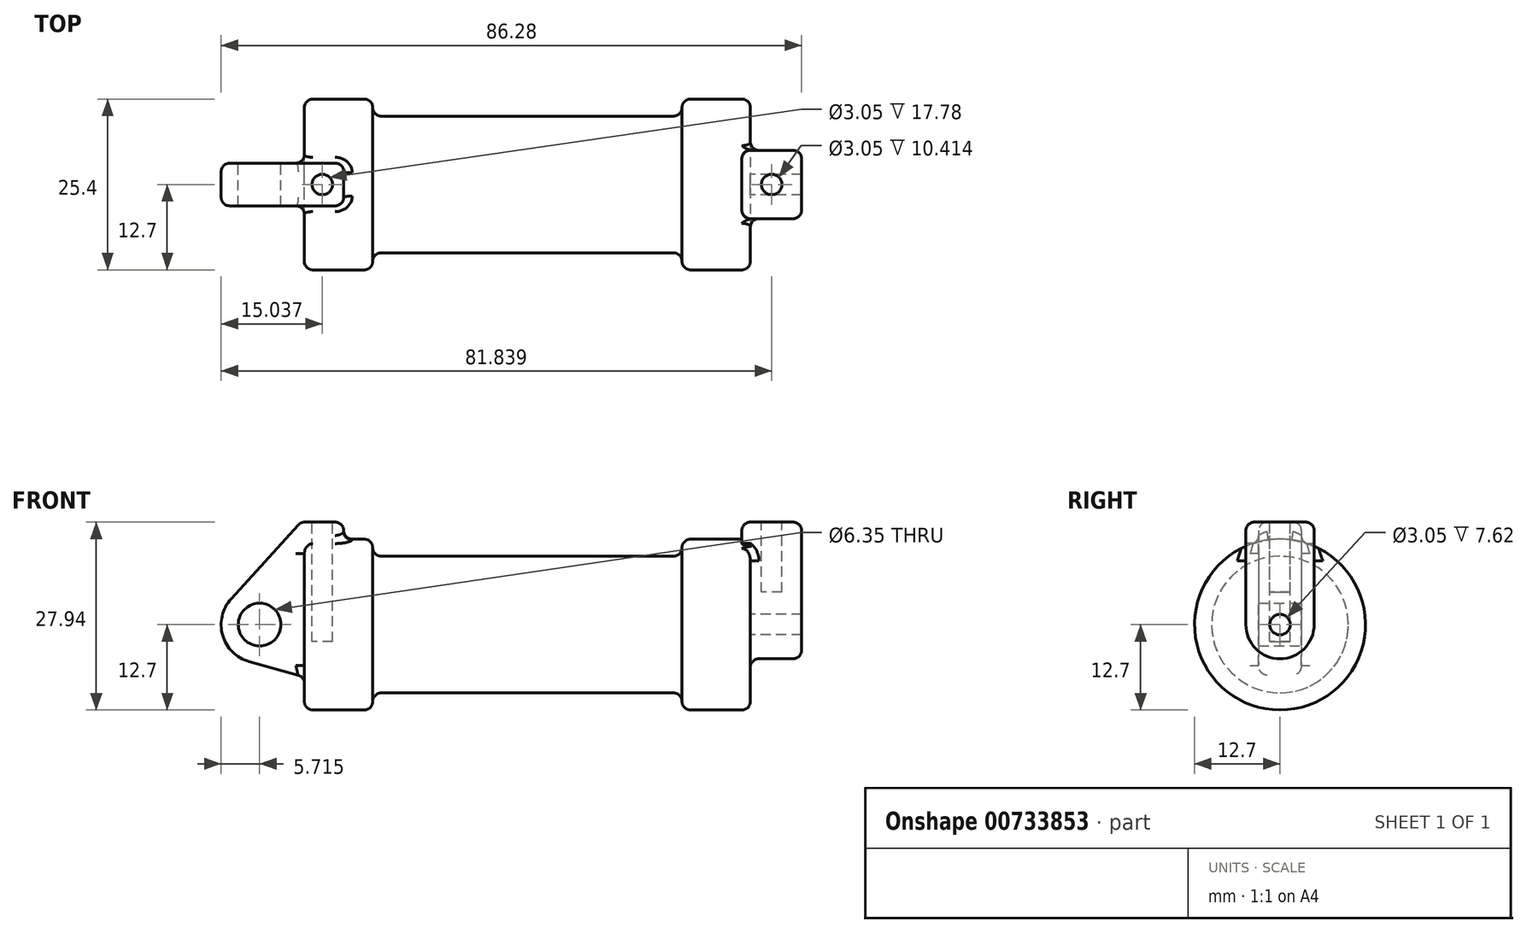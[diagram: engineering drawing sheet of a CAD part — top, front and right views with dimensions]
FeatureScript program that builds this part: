
annotation { "Feature Type Name" : "Feature", "Feature Type Description" : "" }
export const myFeature = defineFeature(function(context is Context, id is Id, definition is map)
    precondition{}
    {
        {
            var Q0;
            Q0=qCreatedBy(makeId("Front.planeOp"),FACE);
            var sketch = newSketch(context, id + "F0", { "sketchPlane" : qUnion([Q0])});
            skLineSegment(sketch, "E0", {"start": v(0, 0) * mm, "end": v(0, 12.7) * mm});
            skLineSegment(sketch, "E1", {"start": v(0, 12.7) * mm, "end": v(10.16, 12.7) * mm});
            skLineSegment(sketch, "E2", {"start": v(10.16, 12.7) * mm, "end": v(10.16, 10.16) * mm});
            skLineSegment(sketch, "E3", {"start": v(10.16, 10.16) * mm, "end": v(56.13, 10.16) * mm});
            skLineSegment(sketch, "E4", {"start": v(56.13, 10.16) * mm, "end": v(56.13, 12.7) * mm});
            skLineSegment(sketch, "E5", {"start": v(56.13, 12.7) * mm, "end": v(66.3, 12.7) * mm});
            skLineSegment(sketch, "E6", {"start": v(66.3, 12.7) * mm, "end": v(66.3, 0) * mm});
            skLineSegment(sketch, "E7", {"start": v(66.3, 0) * mm, "end": v(0, 0) * mm});
            skLineSegment(sketch, "E8", {"start": v(5.84, 15.24) * mm, "end": v(-0.5, 15.24) * mm});
            skLineSegment(sketch, "E9", {"start": v(-0.5, 15.24) * mm, "end": v(-10.88, 3.85) * mm});
            skLineSegment(sketch, "E10", {"start": v(0, 0) * mm, "end": v(-6.65, 0) * mm});
            skCircle(sketch, "E11", {"center": v(-6.65, 0) * mm, "radius": 5.72 * mm});
            skCircle(sketch, "E12", {"center": v(-6.65, 0) * mm, "radius": 3.18 * mm});
            skLineSegment(sketch, "E13", {"start": v(5.84, 15.24) * mm, "end": v(5.84, -9.4) * mm});
            skLineSegment(sketch, "E14", {"start": v(5.84, -9.4) * mm, "end": v(-8.18, -5.5) * mm});
            skSolve(sketch);
        }
        {
            var Q0;
            {var subQ0=sQuery(id+"F0.wireOp",EDGE,"E0");Q0=makeQuery(id+"F0.imprint","IMPRINT",FACE,{"disambiguationData":[TD([[makeQuery(id+"F0.imprint","IMPRINT",EDGE,{"derivedFrom":subQ0}),-1.0]])]});}
            var Q1;
            {var subQ0=sQuery(id+"F0.wireOp",EDGE,"E2");Q1=makeQuery(id+"F0.imprint","IMPRINT",FACE,{"disambiguationData":[TD([[makeQuery(id+"F0.imprint","IMPRINT",EDGE,{"derivedFrom":subQ0}),-1.0]])]});}
            var Q2;
            Q2=sQuery(id+"F0.wireOp",EDGE,"E10");
            revolve(context, id + "F1", {"surfaceOperationType" : NewSurfaceOperationType.NEW, "entities" : qUnion([Q0, Q1]), "axis" : qUnion([Q2]), "revolveType" : RevolveType.FULL});
        }
        {
            var Q0;
            {var subQ0=sQuery(id+"F0.wireOp",EDGE,"E0");Q0=makeQuery(id+"F0.imprint","IMPRINT",FACE,{"disambiguationData":[TD([[makeQuery(id+"F0.imprint","IMPRINT",EDGE,{"derivedFrom":subQ0}),-1.0]])]});}
            var Q1;
            {var subQ1=sQuery(id+"F0.wireOp",EDGE,"E0");Q1=makeQuery(id+"F0.imprint","IMPRINT",FACE,{"disambiguationData":[TD([[makeQuery(id+"F0.imprint","IMPRINT",EDGE,{"derivedFrom":subQ1}),1.0]])]});}
            var Q2;
            {var subQ5=sQuery(id+"F0.wireOp",EDGE,"E12");Q2=makeQuery(id+"F0.imprint","IMPRINT",FACE,{"disambiguationData":[TD([[makeQuery(id+"F0.imprint","IMPRINT",EDGE,{"derivedFrom":subQ5}),-1.0]])]});}
            var Q3;
            {var subQ0=sQuery(id+"F0.wireOp",EDGE,"E14");Q3=makeQuery(id+"F0.imprint","IMPRINT",FACE,{"disambiguationData":[TD([[makeQuery(id+"F0.imprint","IMPRINT",EDGE,{"derivedFrom":subQ0}),-1.0]])]});}
            extrude(context, id + "F2", {"entities" : qUnion([Q0, Q1, Q2, Q3]), "operationType" : NewBodyOperationType.ADD, "endBound" : BoundingType.SYMMETRIC, "depth" : 6.35 * mm, "offsetDistance" : 25.4 * mm});
        }
        {
            var Q0;
            Q0=makeQuery(id+"F1.opRevolve","SWEPT_FACE",FACE,{"disambiguationData":[OSD([sQuery(id+"F0.wireOp",EDGE,"E6")])]});
            var sketch = newSketch(context, id + "F3", { "sketchPlane" : qUnion([Q0])});
            skCircle(sketch, "E15", {"center": v(0, 0) * mm, "radius": 1.52 * mm});
            skCircle(sketch, "E16", {"center": v(0, 0) * mm, "radius": 5.08 * mm});
            skLineSegment(sketch, "E17", {"start": v(5.08, 0) * mm, "end": v(5.08, 15.24) * mm});
            skLineSegment(sketch, "E18", {"start": v(5.08, 15.24) * mm, "end": v(-5.08, 15.24) * mm});
            skLineSegment(sketch, "E19", {"start": v(-5.08, 15.24) * mm, "end": v(-5.08, 0) * mm});
            skSolve(sketch);
        }
        {
            var Q0;
            Q0=makeQuery(id+"F3.imprint","IMPRINT",FACE,{"disambiguationData":[TD([[makeQuery(id+"F3.imprint","IMPRINT",EDGE,{"derivedFrom":sQuery(id+"F3.wireOp",EDGE,"E15")}),-1.0]])]});
            var Q1;
            {var subQ0=sQuery(id+"F3.wireOp",EDGE,"E18");Q1=makeQuery(id+"F3.imprint","IMPRINT",FACE,{"disambiguationData":[TD([[makeQuery(id+"F3.imprint","IMPRINT",EDGE,{"derivedFrom":subQ0}),1.0]])]});}
            var Q2;
            {var subQ0=sQuery(id+"F3.wireOp",EDGE,"E17");var subQ1=sQuery(id+"F3.wireOp",EDGE,"E16");var subQ2=makeQuery(id+"F3.imprint","INTERSECT",VERTEX,{"derivedFrom":[subQ1,subQ0]});Q2=makeQuery(id+"F3.imprint","IMPRINT",FACE,{"disambiguationData":[TD([[makeQuery(id+"F3.imprint","IMPRINT",EDGE,{"disambiguationData":[TD([[subQ2,-1.0]])],"derivedFrom":subQ1}),-1.0]])]});}
            extrude(context, id + "F4", {"entities" : qUnion([Q0, Q1, Q2]), "operationType" : NewBodyOperationType.ADD, "depth" : 7.62 * mm, "offsetDistance" : 25.4 * mm, "hasSecondDirection" : true, "secondDirectionOppositeDirection" : true, "secondDirectionDepth" : 1.27 * mm});
        }
        {
            var Q0;
            Q0=makeQuery(id+"F4.opExtrude","SWEPT_FACE",FACE,{"disambiguationData":[OSD([sQuery(id+"F3.wireOp",EDGE,"E18")])]});
            var sketch = newSketch(context, id + "F5", { "sketchPlane" : qUnion([Q0])});
            skCircle(sketch, "E20", {"center": v(69.47, 0) * mm, "radius": 1.52 * mm});
            skPoint(sketch, "E20.centerSnap0", {"position": v(65.02, 0) * mm});
            skPoint(sketch, "E20.centerSnap1", {"position": v(69.47, 5.08) * mm});
            skSolve(sketch);
        }
        {
            var Q0;
            Q0=makeQuery(id+"F2.opExtrude","SWEPT_FACE",FACE,{"disambiguationData":[OSD([sQuery(id+"F0.wireOp",EDGE,"E8")])]});
            var sketch = newSketch(context, id + "F6", { "sketchPlane" : qUnion([Q0])});
            skCircle(sketch, "E21", {"center": v(2.67, 0) * mm, "radius": 1.52 * mm});
            skPoint(sketch, "E21.centerSnap0", {"position": v(5.84, 0) * mm});
            skPoint(sketch, "E21.centerSnap1", {"position": v(2.67, 3.18) * mm});
            skSolve(sketch);
        }
        {
            var Q0;
            Q0=makeQuery(id+"F6.imprint","IMPRINT",FACE,{"disambiguationData":[TD([[makeQuery(id+"F6.imprint","IMPRINT",EDGE,{"derivedFrom":sQuery(id+"F6.wireOp",EDGE,"E21")}),1.0]])]});
            extrude(context, id + "F7", {"entities" : qUnion([Q0]), "operationType" : NewBodyOperationType.REMOVE, "oppositeDirection" : true, "depth" : 17.78 * mm, "offsetDistance" : 25.4 * mm});
        }
        {
            var Q0;
            Q0=makeQuery(id+"F5.imprint","IMPRINT",FACE,{"disambiguationData":[TD([[makeQuery(id+"F5.imprint","IMPRINT",EDGE,{"derivedFrom":sQuery(id+"F5.wireOp",EDGE,"E20")}),1.0]])]});
            extrude(context, id + "F8", {"entities" : qUnion([Q0]), "operationType" : NewBodyOperationType.REMOVE, "oppositeDirection" : true, "depth" : 10.4 * mm, "offsetDistance" : 25.4 * mm});
        }
        {
            var Q0;
            Q0=makeQuery(id+"F1.opRevolve","SWEPT_EDGE",EDGE,{"disambiguationData":[OSD([sQuery(id+"F0.wireOp",EDGE,"E2"),sQuery(id+"F0.wireOp",EDGE,"E3")])]});
            var Q1;
            Q1=makeQuery(id+"F1.opRevolve","SWEPT_EDGE",EDGE,{"disambiguationData":[OSD([sQuery(id+"F0.wireOp",EDGE,"E1"),sQuery(id+"F0.wireOp",EDGE,"E2")])]});
            var Q2;
            Q2=makeQuery(id+"F1.opRevolve","SWEPT_EDGE",EDGE,{"disambiguationData":[OSD([sQuery(id+"F0.wireOp",EDGE,"E0"),sQuery(id+"F0.wireOp",EDGE,"E1")])]});
            var Q3;
            Q3=makeQuery(id+"F1.opRevolve","SWEPT_EDGE",EDGE,{"disambiguationData":[OSD([sQuery(id+"F0.wireOp",EDGE,"E3"),sQuery(id+"F0.wireOp",EDGE,"E4")])]});
            var Q4;
            Q4=makeQuery(id+"F1.opRevolve","SWEPT_EDGE",EDGE,{"disambiguationData":[OSD([sQuery(id+"F0.wireOp",EDGE,"E4"),sQuery(id+"F0.wireOp",EDGE,"E5")])]});
            var Q5;
            Q5=makeQuery(id+"F1.opRevolve","SWEPT_EDGE",EDGE,{"disambiguationData":[OSD([sQuery(id+"F0.wireOp",EDGE,"E5"),sQuery(id+"F0.wireOp",EDGE,"E6")])]});
            fillet(context, id + "F9", {"entities" : qUnion([Q0, Q1, Q2, Q3, Q4, Q5]), "radius" : 1.27 * mm, "tangentPropagation" : true, "allowEdgeOverflow" : false});
        }
        {
            var Q0;
            Q0=makeQuery(id+"F2.boolean.opBoolean","INTERSECT",EDGE,{"derivedFrom":[makeQuery(id+"F1.opRevolve","SWEPT_FACE",FACE,{"disambiguationData":[OSD([sQuery(id+"F0.wireOp",EDGE,"E1")])]}),makeQuery(id+"F2.opExtrude","CAP_FACE",FACE,{"disambiguationData":[OSD([sQuery(id+"F0.wireOp",EDGE,"E8"),sQuery(id+"F0.wireOp",EDGE,"E9"),sQuery(id+"F0.wireOp",EDGE,"E11"),sQuery(id+"F0.wireOp",EDGE,"E12"),sQuery(id+"F0.wireOp",EDGE,"E13"),sQuery(id+"F0.wireOp",EDGE,"E14")])],"isStart":true})]});
            var Q1;
            Q1=makeQuery(id+"F2.boolean.opBoolean","INTERSECT",EDGE,{"derivedFrom":[makeQuery(id+"F1.opRevolve","SWEPT_FACE",FACE,{"disambiguationData":[OSD([sQuery(id+"F0.wireOp",EDGE,"E1")])]}),makeQuery(id+"F2.opExtrude","SWEPT_FACE",FACE,{"disambiguationData":[OSD([sQuery(id+"F0.wireOp",EDGE,"E13")])]})]});
            var Q2;
            Q2=makeQuery(id+"F2.boolean.opBoolean","INTERSECT",EDGE,{"derivedFrom":[makeQuery(id+"F1.opRevolve","SWEPT_FACE",FACE,{"disambiguationData":[OSD([sQuery(id+"F0.wireOp",EDGE,"E1")])]}),makeQuery(id+"F2.opExtrude","CAP_FACE",FACE,{"disambiguationData":[OSD([sQuery(id+"F0.wireOp",EDGE,"E8"),sQuery(id+"F0.wireOp",EDGE,"E9"),sQuery(id+"F0.wireOp",EDGE,"E11"),sQuery(id+"F0.wireOp",EDGE,"E12"),sQuery(id+"F0.wireOp",EDGE,"E13"),sQuery(id+"F0.wireOp",EDGE,"E14")])],"isStart":false})]});
            var Q3;
            Q3=makeQuery(id+"F2.boolean.opBoolean","INTERSECT",EDGE,{"derivedFrom":[makeQuery(id+"F1.opRevolve","SWEPT_FACE",FACE,{"disambiguationData":[OSD([sQuery(id+"F0.wireOp",EDGE,"E0")])]}),makeQuery(id+"F2.opExtrude","SWEPT_FACE",FACE,{"disambiguationData":[OSD([sQuery(id+"F0.wireOp",EDGE,"E14")])]})]});
            var Q4;
            Q4=makeQuery(id+"F2.opExtrude","CAP_EDGE",EDGE,{"disambiguationData":[OSD([sQuery(id+"F0.wireOp",EDGE,"E14")])],"isStart":false});
            var Q5;
            Q5=makeQuery(id+"F2.opExtrude","CAP_EDGE",EDGE,{"disambiguationData":[OSD([sQuery(id+"F0.wireOp",EDGE,"E14")])],"isStart":true});
            var Q6;
            Q6=makeQuery(id+"F2.opExtrude","CAP_EDGE",EDGE,{"disambiguationData":[OSD([sQuery(id+"F0.wireOp",EDGE,"E8")])],"isStart":false});
            var Q7;
            Q7=makeQuery(id+"F2.opExtrude","CAP_EDGE",EDGE,{"disambiguationData":[OSD([sQuery(id+"F0.wireOp",EDGE,"E8")])],"isStart":true});
            var Q8;
            Q8=makeQuery(id+"F2.opExtrude","SWEPT_EDGE",EDGE,{"disambiguationData":[OSD([sQuery(id+"F0.wireOp",EDGE,"E8"),sQuery(id+"F0.wireOp",EDGE,"E13")])]});
            var Q9;
            Q9=makeQuery(id+"F2.opExtrude","SWEPT_EDGE",EDGE,{"disambiguationData":[OSD([sQuery(id+"F0.wireOp",EDGE,"E8"),sQuery(id+"F0.wireOp",EDGE,"E9")])]});
            var Q10;
            Q10=makeQuery(id+"F2.opExtrude","CAP_EDGE",EDGE,{"disambiguationData":[OSD([sQuery(id+"F0.wireOp",EDGE,"E13")])],"isStart":false});
            var Q11;
            Q11=makeQuery(id+"F2.opExtrude","CAP_EDGE",EDGE,{"disambiguationData":[OSD([sQuery(id+"F0.wireOp",EDGE,"E13")])],"isStart":true});
            fillet(context, id + "F10", {"entities" : qUnion([Q0, Q1, Q2, Q3, Q4, Q5, Q6, Q7, Q8, Q9, Q10, Q11]), "radius" : 1.27 * mm, "tangentPropagation" : true, "allowEdgeOverflow" : false});
        }
        {
            var Q0;
            Q0=makeQuery(id+"F4.opExtrude","CAP_EDGE",EDGE,{"disambiguationData":[OSD([sQuery(id+"F3.wireOp",EDGE,"E16")])],"isStart":false});
            var Q1;
            Q1=makeQuery(id+"F4.opExtrude","SWEPT_EDGE",EDGE,{"disambiguationData":[OSD([sQuery(id+"F3.wireOp",EDGE,"E17"),sQuery(id+"F3.wireOp",EDGE,"E18")])]});
            var Q2;
            Q2=makeQuery(id+"F4.opExtrude","CAP_EDGE",EDGE,{"disambiguationData":[OSD([sQuery(id+"F3.wireOp",EDGE,"E18")])],"isStart":false});
            var Q3;
            Q3=makeQuery(id+"F4.opExtrude","SWEPT_EDGE",EDGE,{"disambiguationData":[OSD([sQuery(id+"F3.wireOp",EDGE,"E18"),sQuery(id+"F3.wireOp",EDGE,"E19")])]});
            var Q4;
            Q4=makeQuery(id+"F4.opExtrude","CAP_EDGE",EDGE,{"disambiguationData":[OSD([sQuery(id+"F3.wireOp",EDGE,"E18")])],"isStart":true});
            var Q5;
            Q5=makeQuery(id+"F9.opFillet","BLEND_EDGE",EDGE,{"blendedFrom":[makeQuery(id+"F1.opRevolve","SWEPT_EDGE",EDGE,{"disambiguationData":[OSD([sQuery(id+"F0.wireOp",EDGE,"E5"),sQuery(id+"F0.wireOp",EDGE,"E6")])]}),makeQuery(id+"F4.opExtrude","SWEPT_FACE",FACE,{"disambiguationData":[OSD([sQuery(id+"F3.wireOp",EDGE,"E19")])]})],"blendedInto":[makeQuery(id+"F4.opExtrude","SWEPT_FACE",FACE,{"disambiguationData":[OSD([sQuery(id+"F3.wireOp",EDGE,"E19")])]})]});
            fillet(context, id + "F11", {"entities" : qUnion([Q0, Q1, Q2, Q3, Q4, Q5]), "radius" : 1.27 * mm, "tangentPropagation" : true, "allowEdgeOverflow" : false});
        }
        {
            var Q0;
            Q0=makeQuery(id+"F4.opExtrude","CAP_EDGE",EDGE,{"disambiguationData":[OSD([sQuery(id+"F3.wireOp",EDGE,"E17")])],"isStart":true});
            var Q1;
            {var subQ0=sQuery(id+"F3.wireOp",EDGE,"E18");Q1=makeQuery(id+"F11.opFillet","BLEND_EDGE",EDGE,{"blendedFrom":[makeQuery(id+"F4.opExtrude","SWEPT_EDGE",EDGE,{"disambiguationData":[OSD([subQ0,sQuery(id+"F3.wireOp",EDGE,"E19")])]}),makeQuery(id+"F4.opExtrude","CAP_EDGE",EDGE,{"disambiguationData":[OSD([subQ0])],"isStart":true})],"blendedInto":[]});}
            fillet(context, id + "F12", {"entities" : qUnion([Q0, Q1]), "radius" : 1.27 * mm, "tangentPropagation" : true, "allowEdgeOverflow" : false});
        }
    });
